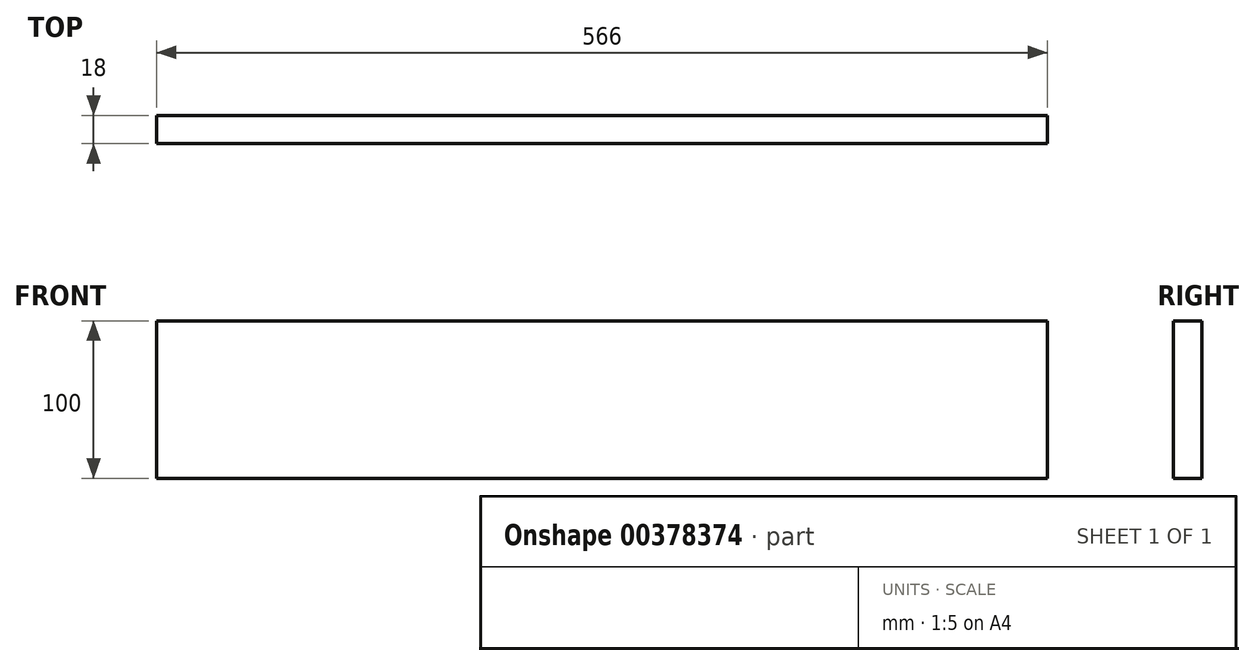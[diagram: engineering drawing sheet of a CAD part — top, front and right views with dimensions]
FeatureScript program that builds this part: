
annotation { "Feature Type Name" : "Feature", "Feature Type Description" : "" }
export const myFeature = defineFeature(function(context is Context, id is Id, definition is map)
    precondition{}
    {
        {
            var Q0;
            Q0=qCreatedBy(makeId("Right.planeOp"),FACE);
            var sketch = newSketch(context, id + "F0", { "sketchPlane" : qUnion([Q0])});
            skLineSegment(sketch, "E0.bottom", {"start": v(9, 50) * mm, "end": v(-9, 50) * mm});
            skLineSegment(sketch, "E0.top", {"start": v(9, -50) * mm, "end": v(-9, -50) * mm});
            skLineSegment(sketch, "E0.left", {"start": v(9, 50) * mm, "end": v(9, -50) * mm});
            skLineSegment(sketch, "E0.right", {"start": v(-9, 50) * mm, "end": v(-9, -50) * mm});
            skPoint(sketch, "E0.middle", {"position": v(0, 0) * mm});
            skSolve(sketch);
        }
        {
            var Q0;
            Q0=qSketchRegion(id+"F0",true);
            extrude(context, id + "F1", {"entities" : qUnion([Q0]), "depth" : 566 * mm});
        }
    });
